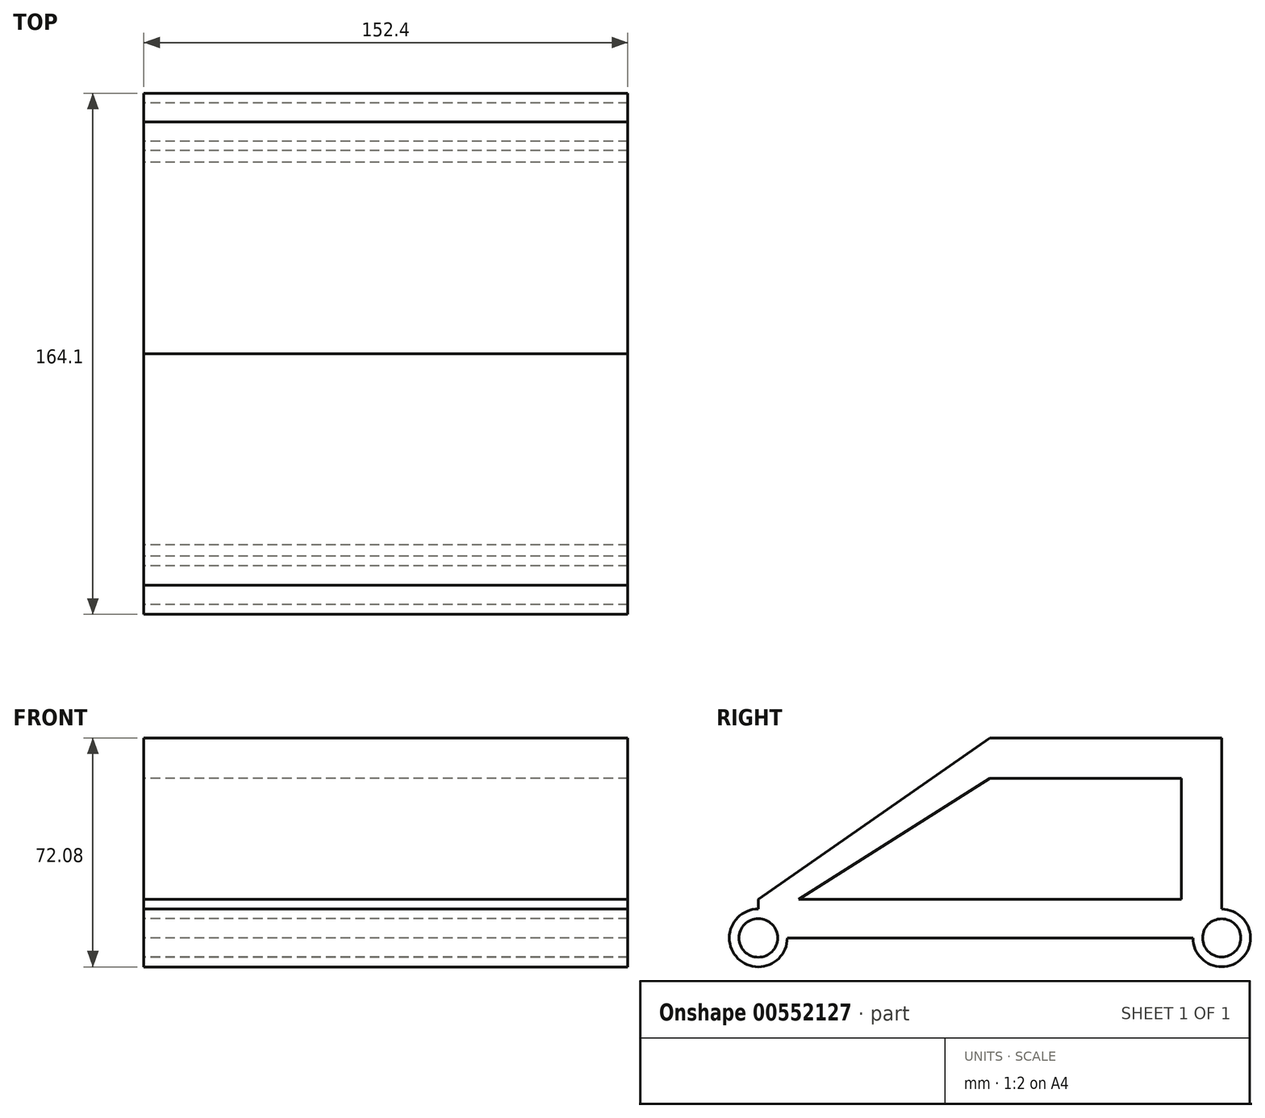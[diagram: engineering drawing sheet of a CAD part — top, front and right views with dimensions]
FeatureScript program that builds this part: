
annotation { "Feature Type Name" : "Feature", "Feature Type Description" : "" }
export const myFeature = defineFeature(function(context is Context, id is Id, definition is map)
    precondition{}
    {
        {
            var Q0;
            Q0=qCreatedBy(makeId("Right.planeOp"),FACE);
            var sketch = newSketch(context, id + "F0", { "sketchPlane" : qUnion([Q0])});
            skLineSegment(sketch, "E0.bottom", {"start": v(60.26, 6.08) * mm, "end": v(-60.26, 6.08) * mm});
            skLineSegment(sketch, "E0.top", {"start": v(60.8, -6.08) * mm, "end": v(-60.8, -6.08) * mm});
            skPoint(sketch, "E0.middle", {"position": v(0, 0) * mm});
            skPoint(sketch, "E1.middle", {"position": v(-72.96, -6.08) * mm});
            skPoint(sketch, "E2.middle", {"position": v(72.96, -6.08) * mm});
            skCircle(sketch, "E3.0", {"center": v(-72.96, -6.08) * mm, "radius": 6.08 * mm});
            skPoint(sketch, "E4.orphan", {"position": v(-60.8, -18.24) * mm});
            skPoint(sketch, "E5.orphan", {"position": v(-85.66, -18.24) * mm});
            skPoint(sketch, "E6.orphan", {"position": v(60.8, -18.24) * mm});
            skPoint(sketch, "E7.orphan", {"position": v(85.66, -18.24) * mm});
            skPoint(sketch, "E8.orphan", {"position": v(85.12, 6.08) * mm});
            skCircle(sketch, "E9.0", {"center": v(72.96, -6.08) * mm, "radius": 6.02 * mm});
            skPoint(sketch, "E10.orphan", {"position": v(-85.12, 6.08) * mm});
            skCircle(sketch, "E11.0", {"center": v(-72.96, -6.08) * mm, "radius": 9.12 * mm});
            skLineSegment(sketch, "E12", {"start": v(-60.8, -6.08) * mm, "end": v(-63.84, -6.08) * mm});
            skLineSegment(sketch, "E13", {"start": v(-72.96, 6.08) * mm, "end": v(-72.96, 3.04) * mm});
            skCircle(sketch, "E14.0", {"center": v(72.96, -6.08) * mm, "radius": 9.06 * mm});
            skLineSegment(sketch, "E15", {"start": v(72.96, 6.08) * mm, "end": v(72.96, 2.98) * mm});
            skLineSegment(sketch, "E16", {"start": v(60.8, -6.08) * mm, "end": v(63.9, -6.08) * mm});
            skLineSegment(sketch, "E17", {"start": v(60.26, 6.08) * mm, "end": v(60.26, 44.18) * mm});
            skLineSegment(sketch, "E18", {"start": v(60.26, 56.88) * mm, "end": v(72.96, 56.88) * mm});
            skLineSegment(sketch, "E19", {"start": v(72.96, 56.88) * mm, "end": v(72.96, 6.08) * mm});
            skLineSegment(sketch, "E20", {"start": v(60.26, 44.18) * mm, "end": v(0, 44.18) * mm});
            skLineSegment(sketch, "E21", {"start": v(60.26, 56.88) * mm, "end": v(0, 56.88) * mm});
            skLineSegment(sketch, "E22", {"start": v(-60.26, 6.08) * mm, "end": v(0, 44.18) * mm});
            skLineSegment(sketch, "E23", {"start": v(0, 56.88) * mm, "end": v(-72.96, 6.08) * mm});
            skSolve(sketch);
        }
        {
            var Q0;
            Q0=makeQuery(id+"F0.imprint","IMPRINT",FACE,{"disambiguationData":[TD([[makeQuery(id+"F0.imprint","IMPRINT",EDGE,{"derivedFrom":sQuery(id+"F0.wireOp",EDGE,"E0.bottom")}),1.0]])]});
            var Q1;
            Q1=makeQuery(id+"F0.imprint","IMPRINT",FACE,{"disambiguationData":[TD([[makeQuery(id+"F0.imprint","IMPRINT",EDGE,{"derivedFrom":sQuery(id+"F0.wireOp",EDGE,"E3.0")}),-1.0]])]});
            var Q2;
            Q2=makeQuery(id+"F0.imprint","IMPRINT",FACE,{"disambiguationData":[TD([[makeQuery(id+"F0.imprint","IMPRINT",EDGE,{"derivedFrom":sQuery(id+"F0.wireOp",EDGE,"E9.0")}),-1.0]])]});
            extrude(context, id + "F1", {"entities" : qUnion([Q0, Q1, Q2]), "endBound" : BoundingType.SYMMETRIC, "depth" : 152.4 * mm, "offsetDistance" : 25.4 * mm});
        }
    });
